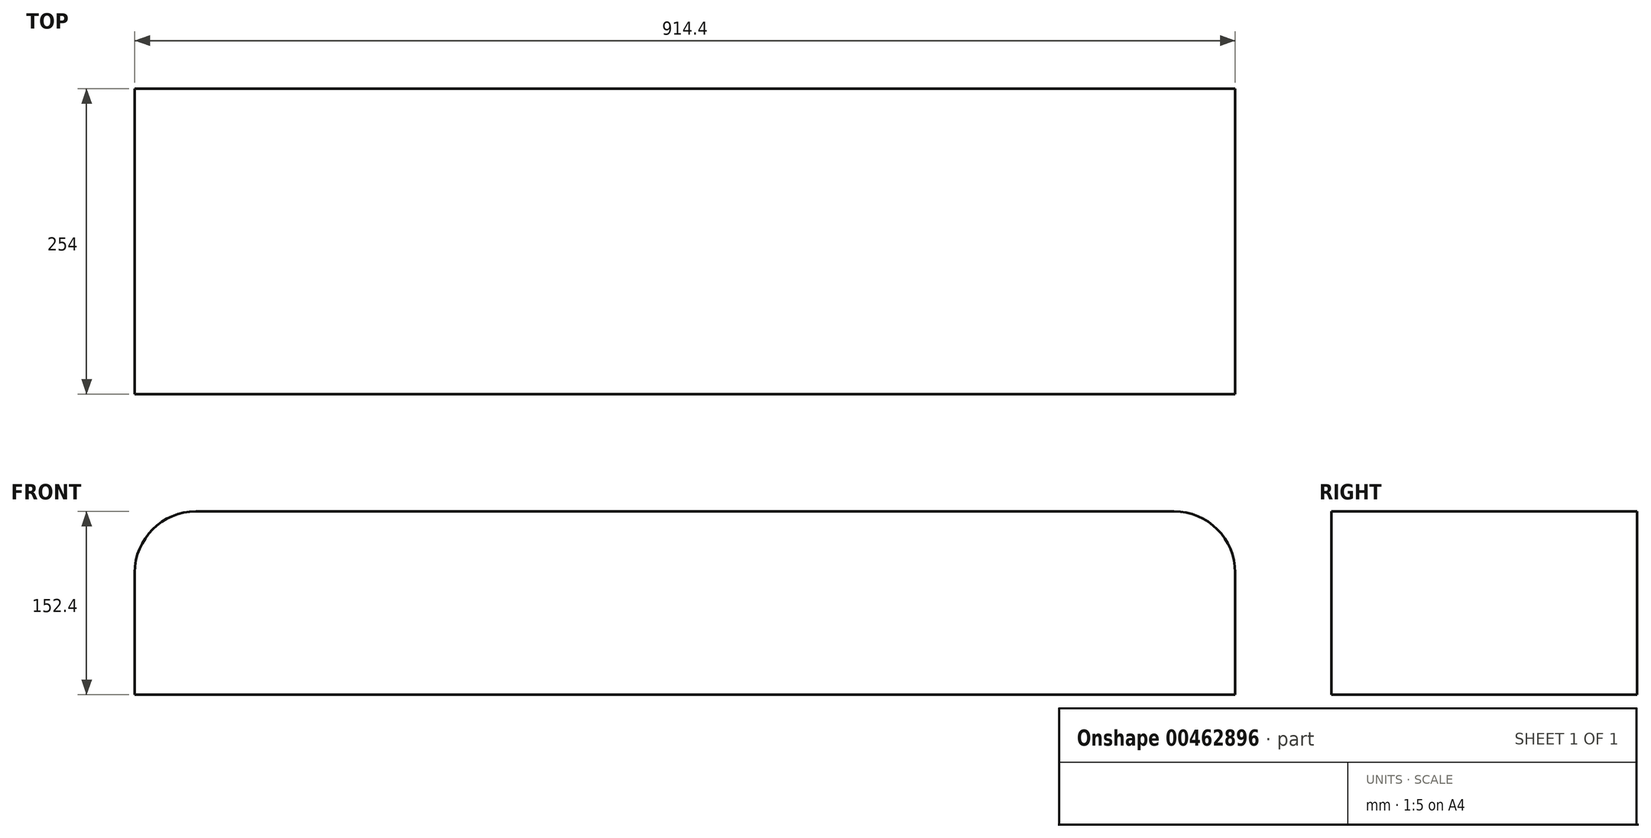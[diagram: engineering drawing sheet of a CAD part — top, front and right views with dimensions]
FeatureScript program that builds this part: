
annotation { "Feature Type Name" : "Feature", "Feature Type Description" : "" }
export const myFeature = defineFeature(function(context is Context, id is Id, definition is map)
    precondition{}
    {
        {
            var Q0;
            Q0=qCreatedBy(makeId("Front.planeOp"),FACE);
            var sketch = newSketch(context, id + "F0", { "sketchPlane" : qUnion([Q0])});
            skLineSegment(sketch, "E0.bottom", {"start": v(0, 0) * mm, "end": v(457.2, 0) * mm});
            skLineSegment(sketch, "E0.right", {"start": v(457.2, 0) * mm, "end": v(457.2, 152.4) * mm});
            skLineSegment(sketch, "E1.bottom", {"start": v(0, 0) * mm, "end": v(-457.2, 0) * mm});
            skLineSegment(sketch, "E1.right", {"start": v(-457.2, 0) * mm, "end": v(-457.2, 152.4) * mm});
            skLineSegment(sketch, "E2", {"start": v(-457.2, 152.4) * mm, "end": v(457.2, 152.4) * mm});
            skSolve(sketch);
        }
        {
            var Q0;
            Q0=makeQuery(id+"F0.imprint","IMPRINT",FACE,{"disambiguationData":[TD([[makeQuery(id+"F0.imprint","IMPRINT",EDGE,{"derivedFrom":sQuery(id+"F0.wireOp",EDGE,"E0.bottom")}),1.0]])]});
            extrude(context, id + "F1", {"entities" : qUnion([Q0]), "oppositeDirection" : true, "depth" : 254 * mm});
        }
        {
            var Q0;
            Q0=makeQuery(id+"F1.opExtrude","SWEPT_EDGE",EDGE,{"disambiguationData":[OSD([sQuery(id+"F0.wireOp",EDGE,"E1.right"),sQuery(id+"F0.wireOp",EDGE,"E2")])]});
            var Q1;
            Q1=makeQuery(id+"F1.opExtrude","SWEPT_EDGE",EDGE,{"disambiguationData":[OSD([sQuery(id+"F0.wireOp",EDGE,"E0.right"),sQuery(id+"F0.wireOp",EDGE,"E2")])]});
            fillet(context, id + "F2", {"entities" : qUnion([Q0, Q1]), "radius" : 50.8 * mm, "tangentPropagation" : true, "allowEdgeOverflow" : false});
        }
    });
